# Revit family: 0054104
name_source: partatom
category: Lighting Fixtures
revit_build: Autodesk Revit 2018 (Build: 20170223_1515(x64)
units: mm (PartAtom-declared; Revit-internal decimal feet)

## family parameters
Cut with Voids When Loaded = No
Host = Face
Light Source = Yes
OmniClass Number = 23.80.70.00
OmniClass Title = Lighting
Part Type = Normal
Room Calculation Point = No
Round Connector Dimension = Use Diameter
Shared = No

## types (1)
- 0054104 START ECO DOWNLIGHT 215 1250LM 830 SRFC
    Apparent Load = 15 VA
    Assembly Code = D5020200
    AssetType = Fixed
    ClassificationName = Uniclass2015
    ClassificationValue = EF_70_80
    Color Filter = 16777215
    Cost = 0 $
    Default Elevation = 1219 mm
    Description = START eco Downlight is an integrated LED surface mounted downlight with built-in non dimmable driver; 15W; 1250Lm; 83Lm/W; 3000K.
    Dimming Lamp Color Temperature Shift = <None>
    DocumentationLiterature = http://www.sylvania-lighting.com
    ElectricShockClassification = 83
    Emit Shape Visible in Rendering = No
    Emit from Circle Diameter = 610 mm
    IfcExportAs = Class II
    IfcExportType = IfcLightFixtureType
    ImpactProtectionIndex = IfcLightFixtureType
    IngressProtection = IfcLightFixtureType
    InputNominalFrequency = 3000
    InputVoltage = 0
    LampColourRenderingIndex = 16500
    LampColourTemperature = LED
    LampMacAdamStep = 80
    LampNominalLuminous = 3000 K
    LightOutputRatio = LED
    LuminaireType = 0
    ManufacturerName = 83 lm/W
    Material = Feilo Sylvania
    Material_1_SYL = <By Category>
    Material_2_SYL = <By Category>
    Material_3_SYL = <By Category>
    Material_4_SYL = <By Category>
    Model = START eco Downlight 215 1250lm 830 Surface
    ModelNumber = 0054104
    ModelReference = START eco Downlight 215 1250lm 830 Surface
    Name = START eco Downlight 215 1250lm 830 Surface
    NominalDepth = 215 mm  [stored 0.705381 ft]
    NominalHeight = 45 mm
    NominalLength = 215 mm  [stored 0.705381 ft]
    Photometric Web File = 0054104.ies
    PowerConsumption = Lighting
    PowerFactor = 0
    Tilt Angle = -90.00°
    Type Image = <None>
    TypeName = START eco Downlight 215 1250lm 830 Surface
    URL = 0.5
    Voltage = 0 V
    WarrantyDescription = http://www.sylvania-lighting.com
    chamfer dia = 191 mm
    lens dia = 172 mm  [stored 0.564304 ft]

note: [stored X ft] marks values corroborated as IEEE doubles in the binary element streams (Revit-internal decimal feet)

## geometry (parser evidence)
native form markers: Sweep x1
no freeform markers — native parametric forms only
